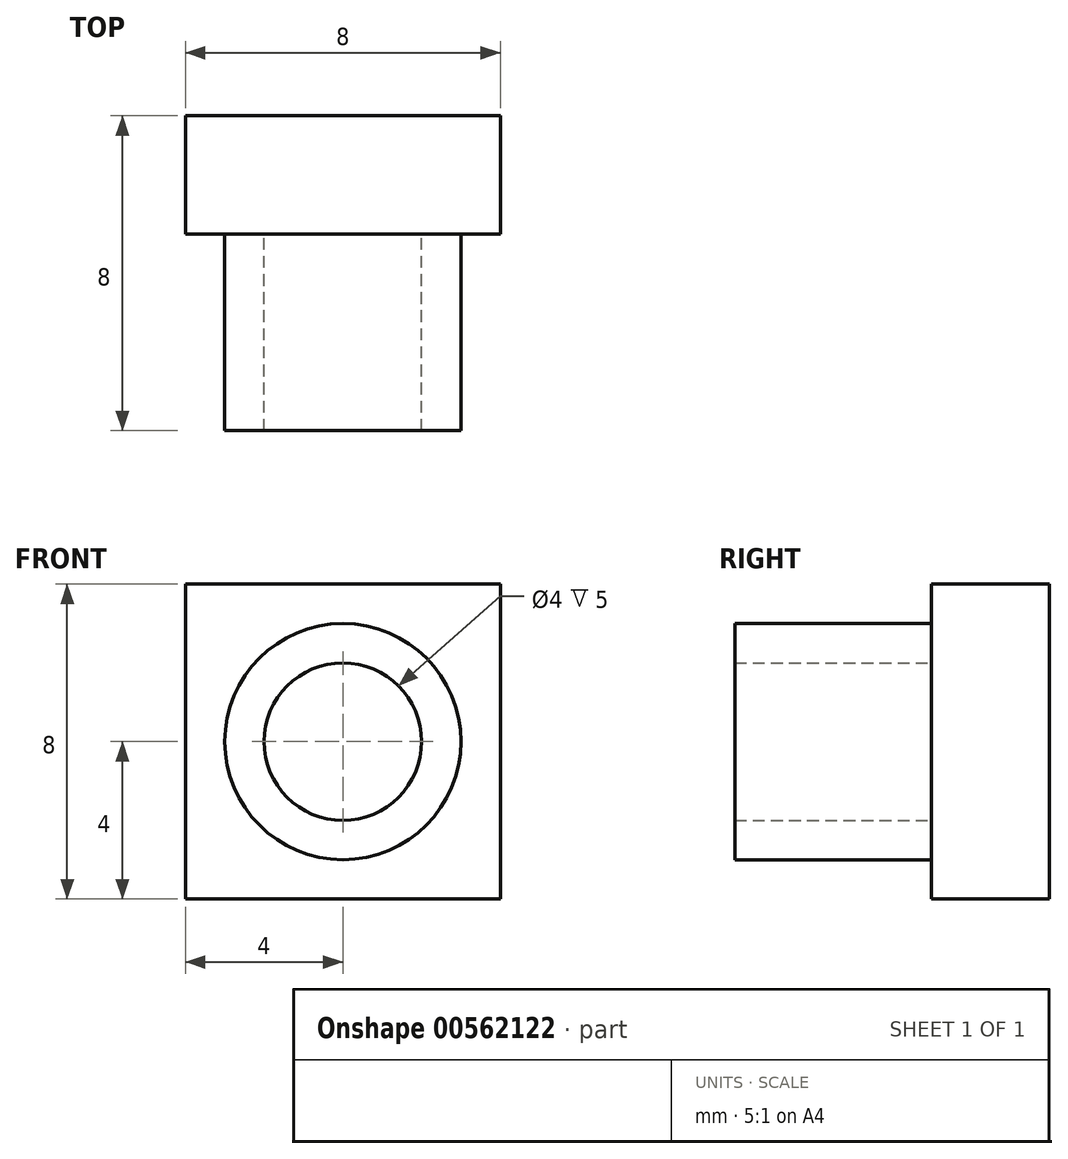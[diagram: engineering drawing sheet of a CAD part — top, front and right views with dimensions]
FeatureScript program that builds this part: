
annotation { "Feature Type Name" : "Feature", "Feature Type Description" : "" }
export const myFeature = defineFeature(function(context is Context, id is Id, definition is map)
    precondition{}
    {
        {
            var Q0;
            Q0=qCreatedBy(makeId("Front.planeOp"),FACE);
            var sketch = newSketch(context, id + "F0", { "sketchPlane" : qUnion([Q0])});
            skLineSegment(sketch, "E0.bottom", {"start": v(4, 4) * mm, "end": v(-4, 4) * mm});
            skLineSegment(sketch, "E0.top", {"start": v(4, -4) * mm, "end": v(-4, -4) * mm});
            skLineSegment(sketch, "E0.left", {"start": v(4, 4) * mm, "end": v(4, -4) * mm});
            skLineSegment(sketch, "E0.right", {"start": v(-4, 4) * mm, "end": v(-4, -4) * mm});
            skPoint(sketch, "E0.middle", {"position": v(0, 0) * mm});
            skSolve(sketch);
        }
        {
            var Q0;
            Q0=makeQuery(id+"F0.imprint","IMPRINT",FACE,{"disambiguationData":[TD([[makeQuery(id+"F0.imprint","IMPRINT",EDGE,{"derivedFrom":sQuery(id+"F0.wireOp",EDGE,"E0.bottom")}),1.0]])]});
            extrude(context, id + "F1", {"entities" : qUnion([Q0]), "depth" : 3 * mm, "offsetDistance" : 25.4 * mm});
        }
        {
            var Q0;
            Q0=makeQuery(id+"F1.opExtrude","CAP_FACE",FACE,{"disambiguationData":[OSD([sQuery(id+"F0.wireOp",EDGE,"E0.bottom"),sQuery(id+"F0.wireOp",EDGE,"E0.top"),sQuery(id+"F0.wireOp",EDGE,"E0.left"),sQuery(id+"F0.wireOp",EDGE,"E0.right")])],"isStart":false});
            var sketch = newSketch(context, id + "F2", { "sketchPlane" : qUnion([Q0])});
            skCircle(sketch, "E1", {"center": v(0, 0) * mm, "radius": 3 * mm});
            skCircle(sketch, "E2", {"center": v(0, 0) * mm, "radius": 2 * mm});
            skSolve(sketch);
        }
        {
            var Q0;
            Q0=makeQuery(id+"F2.imprint","IMPRINT",FACE,{"disambiguationData":[TD([[makeQuery(id+"F2.imprint","IMPRINT",EDGE,{"derivedFrom":sQuery(id+"F2.wireOp",EDGE,"E1")}),1.0]])]});
            extrude(context, id + "F3", {"entities" : qUnion([Q0]), "operationType" : NewBodyOperationType.ADD, "depth" : 5 * mm, "offsetDistance" : 25.4 * mm});
        }
    });
